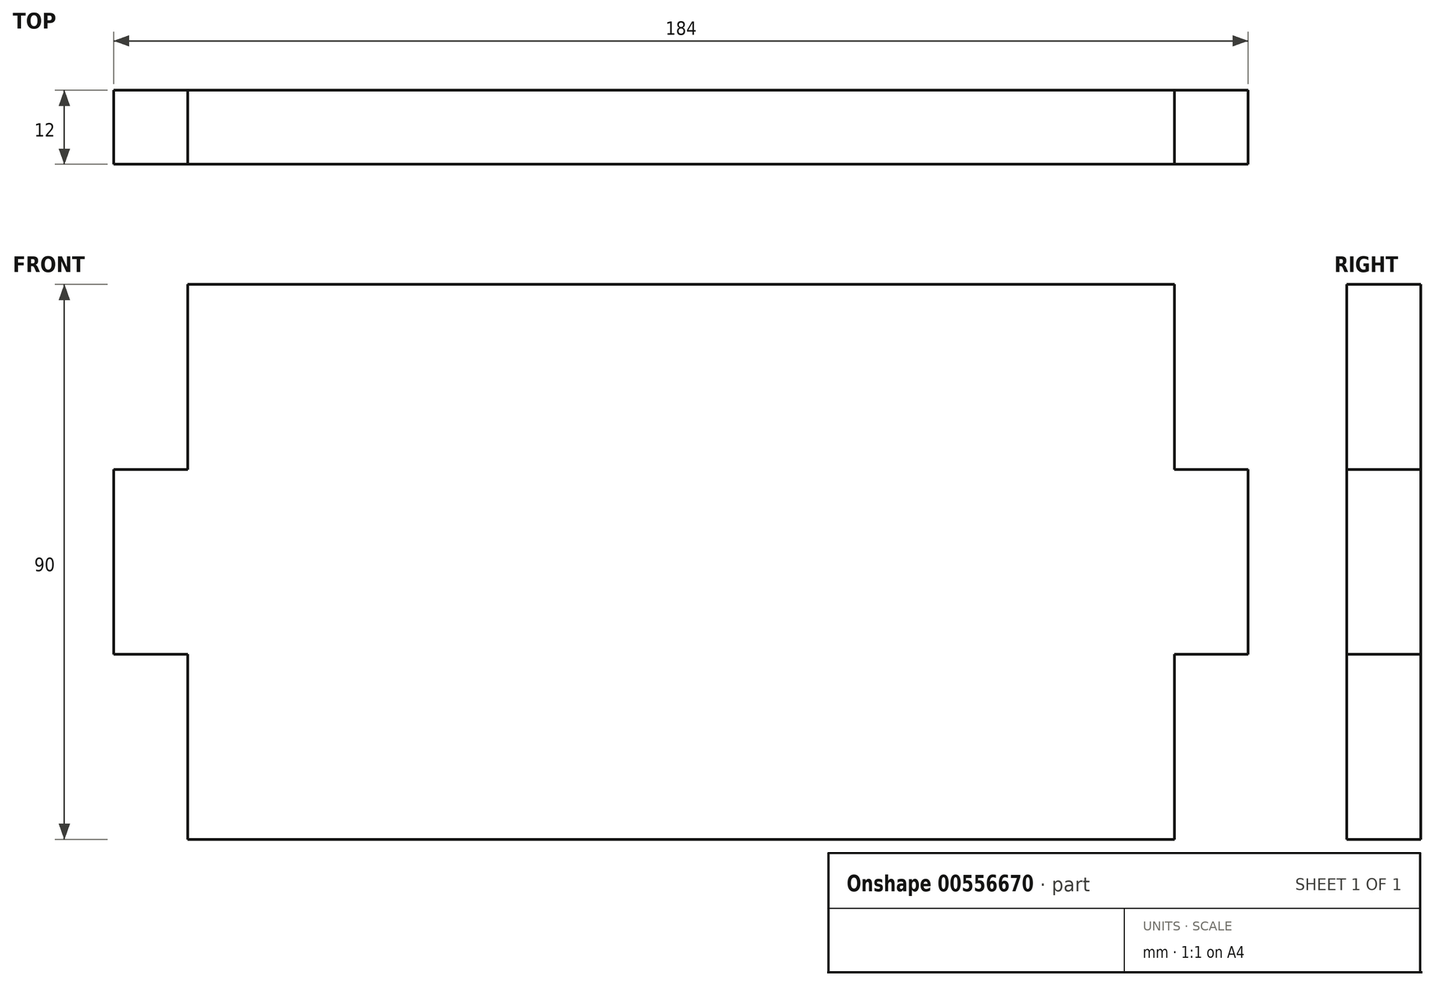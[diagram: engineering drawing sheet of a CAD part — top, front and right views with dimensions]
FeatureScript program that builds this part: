
annotation { "Feature Type Name" : "Feature", "Feature Type Description" : "" }
export const myFeature = defineFeature(function(context is Context, id is Id, definition is map)
    precondition{}
    {
        {
            var Q0;
            Q0=qCreatedBy(makeId("Front.planeOp"),FACE);
            var sketch = newSketch(context, id + "F0", { "sketchPlane" : qUnion([Q0])});
            skLineSegment(sketch, "E0", {"start": v(0, 0) * mm, "end": v(0, 30) * mm});
            skLineSegment(sketch, "E1", {"start": v(0, 30) * mm, "end": v(-12, 30) * mm});
            skLineSegment(sketch, "E2", {"start": v(-12, 30) * mm, "end": v(-12, 60) * mm});
            skLineSegment(sketch, "E3", {"start": v(-12, 60) * mm, "end": v(0, 60) * mm});
            skLineSegment(sketch, "E4", {"start": v(0, 60) * mm, "end": v(0, 90) * mm});
            skLineSegment(sketch, "E5", {"start": v(0, 90) * mm, "end": v(80, 90) * mm});
            skLineSegment(sketch, "E6", {"start": v(80, 90) * mm, "end": v(80, 0) * mm, "construction": true});
            skLineSegment(sketch, "E7", {"start": v(80, 0) * mm, "end": v(0, 0) * mm});
            skLineSegment(sketch, "E8.MirrorCS", {"start": v(160, 30) * mm, "end": v(172, 30) * mm});
            skLineSegment(sketch, "E9.MirrorCS", {"start": v(172, 30) * mm, "end": v(172, 60) * mm});
            skLineSegment(sketch, "E10.MirrorCS", {"start": v(160, 60) * mm, "end": v(160, 90) * mm});
            skLineSegment(sketch, "E11.MirrorCS", {"start": v(160, 0) * mm, "end": v(160, 30) * mm});
            skLineSegment(sketch, "E12.MirrorCS", {"start": v(160, 90) * mm, "end": v(80, 90) * mm});
            skLineSegment(sketch, "E13.MirrorCS", {"start": v(172, 60) * mm, "end": v(160, 60) * mm});
            skLineSegment(sketch, "E14.MirrorCS", {"start": v(80, 0) * mm, "end": v(160, 0) * mm});
            skSolve(sketch);
        }
        {
            var Q0;
            Q0 = qSketchRegion(id + "F0", true);
            extrude(context, id + "F1", {"entities" : qUnion([Q0]), "endBound" : BoundingType.SYMMETRIC, "depth" : 12 * mm, "offsetDistance" : 25 * mm});
        }
    });
